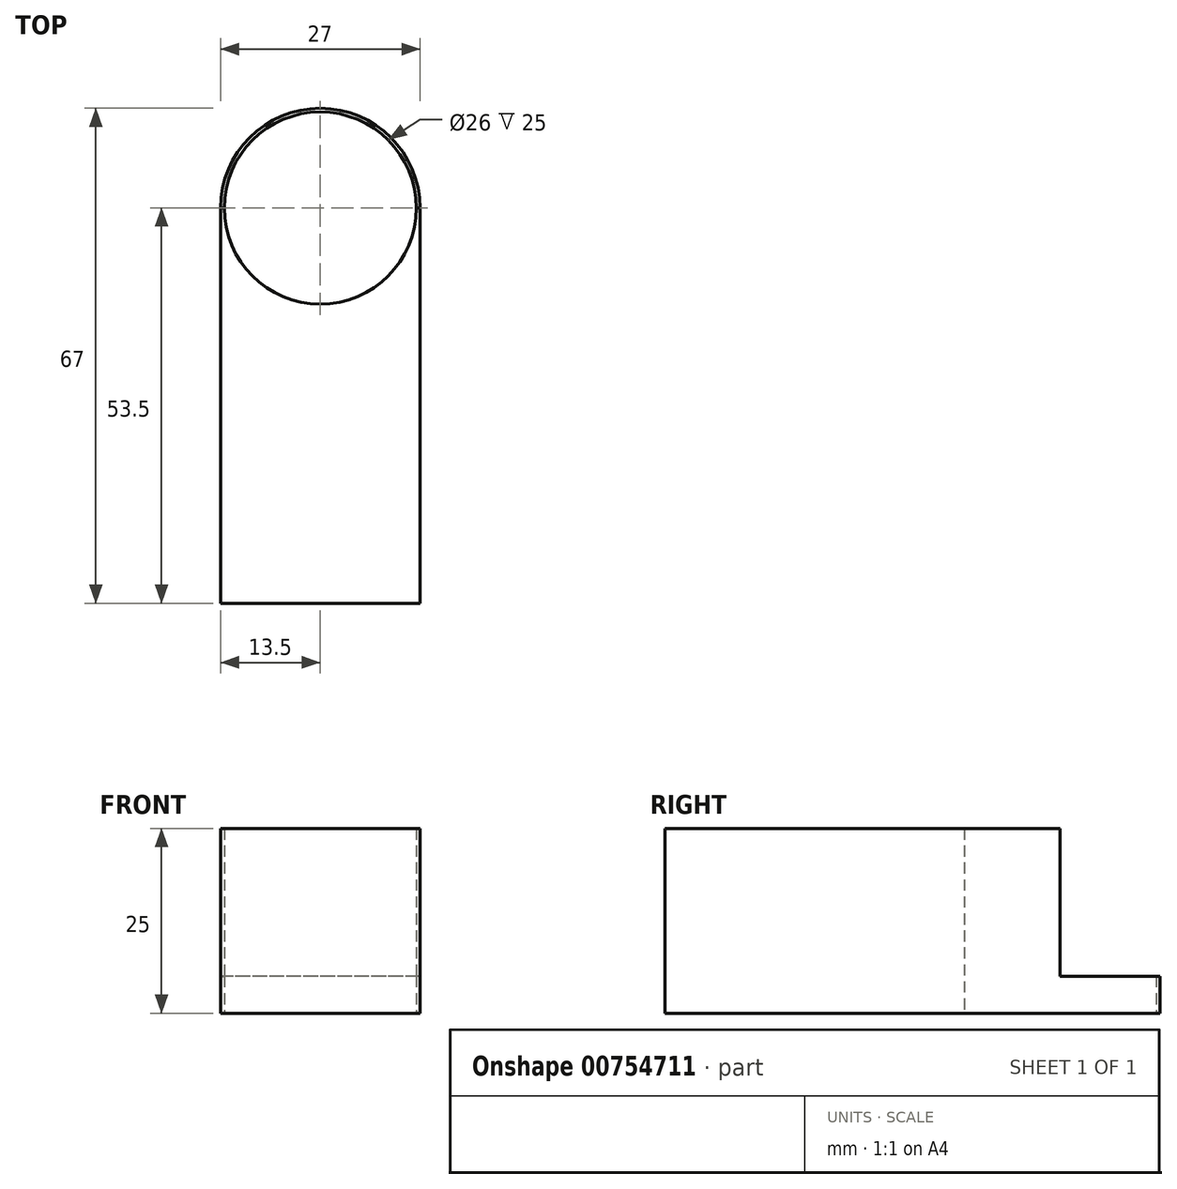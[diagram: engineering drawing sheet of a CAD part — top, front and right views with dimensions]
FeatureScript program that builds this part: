
annotation { "Feature Type Name" : "Feature", "Feature Type Description" : "" }
export const myFeature = defineFeature(function(context is Context, id is Id, definition is map)
    precondition{}
    {
        {
            var Q0;
            Q0=qCreatedBy(makeId("Top.planeOp"),FACE);
            var sketch = newSketch(context, id + "F0", { "sketchPlane" : qUnion([Q0])});
            skCircle(sketch, "E0", {"center": v(0, 0) * mm, "radius": 13.5 * mm});
            skLineSegment(sketch, "E1", {"start": v(-13.5, 0) * mm, "end": v(-13.5, -53.5) * mm});
            skLineSegment(sketch, "E2", {"start": v(13.5, 0) * mm, "end": v(13.5, -53.5) * mm});
            skLineSegment(sketch, "E3", {"start": v(13.5, -53.5) * mm, "end": v(-13.5, -53.5) * mm});
            skCircle(sketch, "E4", {"center": v(0, 0) * mm, "radius": 13 * mm});
            skLineSegment(sketch, "E5", {"start": v(0, -13.5) * mm, "end": v(0, -53.5) * mm});
            skLineSegment(sketch, "E6", {"start": v(-13.5, 0) * mm, "end": v(-13, 0) * mm});
            skLineSegment(sketch, "E7", {"start": v(13.5, 0) * mm, "end": v(13, 0) * mm});
            skSolve(sketch);
        }
        {
            var Q0;
            {var subQ0=sQuery(id+"F0.wireOp",EDGE,"E6");Q0=makeQuery(id+"F0.imprint","IMPRINT",FACE,{"disambiguationData":[TD([[makeQuery(id+"F0.imprint","IMPRINT",EDGE,{"derivedFrom":subQ0}),-1.0]])]});}
            var Q1;
            {var subQ0=sQuery(id+"F0.wireOp",EDGE,"E2");Q1=makeQuery(id+"F0.imprint","IMPRINT",FACE,{"disambiguationData":[TD([[makeQuery(id+"F0.imprint","IMPRINT",EDGE,{"derivedFrom":subQ0}),-1.0]])]});}
            var Q2;
            {var subQ0=sQuery(id+"F0.wireOp",EDGE,"E1");Q2=makeQuery(id+"F0.imprint","IMPRINT",FACE,{"disambiguationData":[TD([[makeQuery(id+"F0.imprint","IMPRINT",EDGE,{"derivedFrom":subQ0}),1.0]])]});}
            extrude(context, id + "F1", {"entities" : qUnion([Q0, Q1, Q2]), "depth" : 25 * mm, "offsetDistance" : 25 * mm});
        }
        {
            var Q0;
            {var subQ0=sQuery(id+"F0.wireOp",EDGE,"E6");Q0=makeQuery(id+"F0.imprint","IMPRINT",FACE,{"disambiguationData":[TD([[makeQuery(id+"F0.imprint","IMPRINT",EDGE,{"derivedFrom":subQ0}),1.0]])]});}
            extrude(context, id + "F2", {"entities" : qUnion([Q0]), "operationType" : NewBodyOperationType.ADD, "depth" : 5 * mm, "offsetDistance" : 25 * mm});
        }
    });
